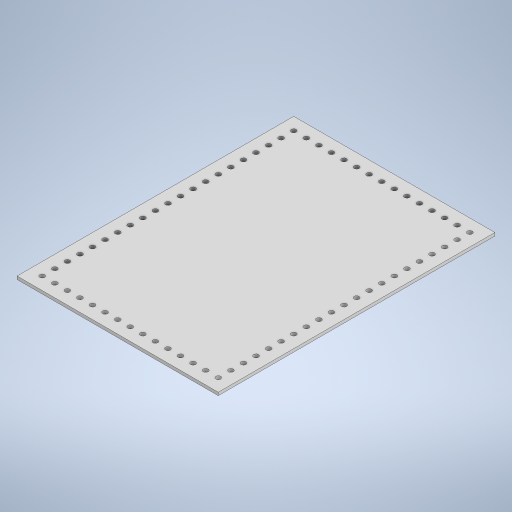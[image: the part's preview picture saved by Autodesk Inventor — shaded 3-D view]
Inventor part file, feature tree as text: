
AUTODESK INVENTOR PART (.ipt)
format: ipt  version: 2023.4 (Build 274418000, 418)  size: 336,384 bytes
history: native  units: in
note: dims shown in document units (in); Inventor stores cm internally (conversion verified against a paired STEP export)
features: sketch x2, sheet_metal_op x1, extrude x1, other x1
ambient origin geometry x8: Origin, YZ Plane, XZ Plane, XY Plane, X Axis, Y Axis, Z Axis, Center Point
bodies: Solid1 (feature_tree)
feature tree (5):
  sheet_metal_op  "Face1"
  extrude  "Extrusion1"  Depth=11.0in
  sketch  "Sketch1"  dims[d0=8.0in d1=11.0in]
  other  "Plate1"
  sketch  "Sketch2"  dims[d2=0.12in d3=0.197in d4=0.5in d5=0.5in d6=5.5118in d8=0.5in d9=0.3937in d11=1.0in d13=0.197in d15=0.5in d16=0.5in d17=7.874in d19=0.5in d20=0.3937in d22=1.0in d24=0.197in d25=0.5in d26=0.5in d27=5.5118in d29=0.5in d30=0.3937in d32=1.0in d34=0.197in d35=0.5in d36=0.5in d37=7.874in d39=0.5in d40=0.3937in d42=1.0in d44=1.0in d45=0.0in]
